# Revit family: ASD Coded Note
name_source: partatom
category: Generic Annotations
revit_build: Autodesk Revit 2013 (Build: 20130531_2115(x64)
units: mm (PartAtom-declared; Revit-internal decimal feet)

## types (10) — shared parameters

## per-type parameters (varying)
| type | Sheet Note | Sheet Note Number | Sheet Type |
| PC Note 1 | DUPLEX RECEPTACLE AND DATA JACK TERMINATED IN CEILING TILE FOR AV PROJECTOR.  INSTALL PROJECTOR MOUNT SUPPLIED BY AV.  FINAL LOCATIONS TBD | 1 | PC |
| FIN Note 1 | CODED NOTE #1 - FINISH | 1 | FINISH |
| RCP Note 1 | CENTER CEILING GRID IN ROOM UON | 1 | RCP |
| RCP Note 2 | INSTALL ACOUSTICAL BATT INSULATION ABOVE THE EMTIRE CEILING OVER THE DEMOUNTABLE PARTITIONS.  THIS INSULATION SHOULD EXTEND 2' BEYOND THE PERIMETER WALLS IN ALL DIRECTIONS. | 2 | RCP |
| DEMO Note 3 | Edit Type to Enter Text | 3 | DEMO |
| DEMO Note 2 | Edit Type to Enter Text | 2 | DEMO |
| FIN Note 3 | CODED NOTE #3 - FINISH PLAN | 3 | FINISH |
| FIN Note 2 | CODED NOTE #2 - FINISH PLAN | 2 | FINISH |
| DEMO Note 1 | Edit Type to Enter Text | 1 | DEMO |
| ADA Note 1 | XXXXXXXXXXXXXXXXXXXXXXXXXXXXXXXXXXXXXXXXXXXXXXXXXXXXXXXXXXXXXXXXXXXXXXXXXXXXXXXXXXXXXXXXXXXXXXXXXXXXXXXXXXXXXXX | 1 | ADA RESTROOM |

## geometry (parser evidence)
native form markers: Sweep x2
no freeform markers — native parametric forms only
